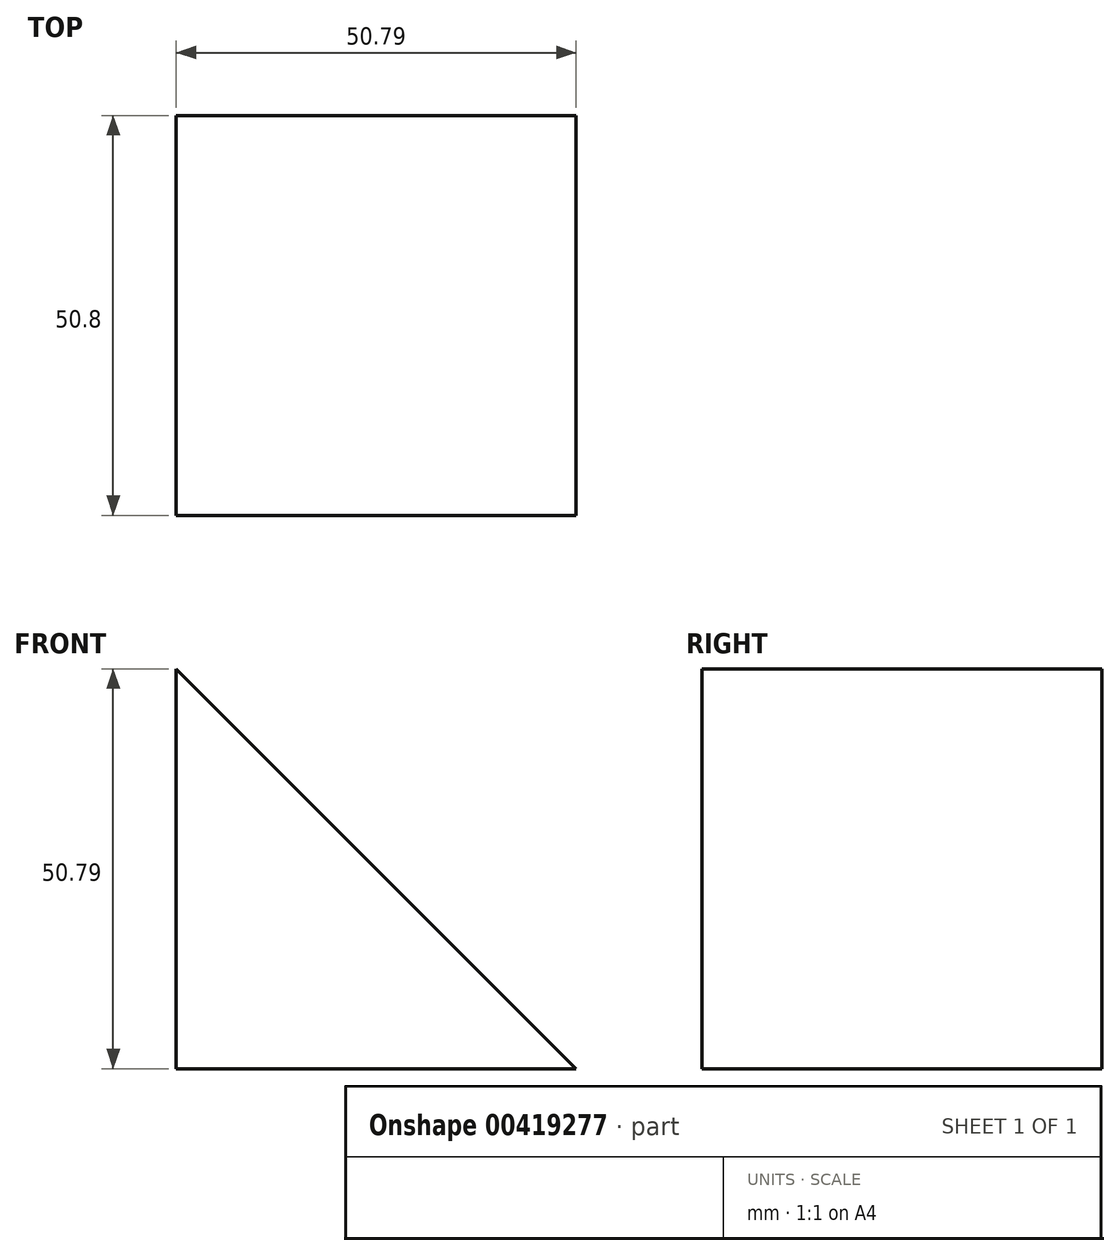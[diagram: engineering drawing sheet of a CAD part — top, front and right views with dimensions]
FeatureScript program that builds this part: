
annotation { "Feature Type Name" : "Feature", "Feature Type Description" : "" }
export const myFeature = defineFeature(function(context is Context, id is Id, definition is map)
    precondition{}
    {
        {
            var Q0;
            Q0=qCreatedBy(makeId("Front.planeOp"),FACE);
            var sketch = newSketch(context, id + "F0", { "sketchPlane" : qUnion([Q0])});
            skLineSegment(sketch, "E0", {"start": v(0, 0) * mm, "end": v(0, 50.8) * mm});
            skLineSegment(sketch, "E1", {"start": v(0, 0) * mm, "end": v(50.8, 0) * mm});
            skLineSegment(sketch, "E2", {"start": v(50.8, 0) * mm, "end": v(0, 50.8) * mm});
            skSolve(sketch);
        }
        {
            var Q0;
            Q0=makeQuery(id+"F0.imprint","IMPRINT",FACE,{"disambiguationData":[TD([[makeQuery(id+"F0.imprint","IMPRINT",EDGE,{"derivedFrom":sQuery(id+"F0.wireOp",EDGE,"E0")}),-1.0]])]});
            extrude(context, id + "F1", {"entities" : qUnion([Q0]), "depth" : 50.8 * mm});
        }
    });
